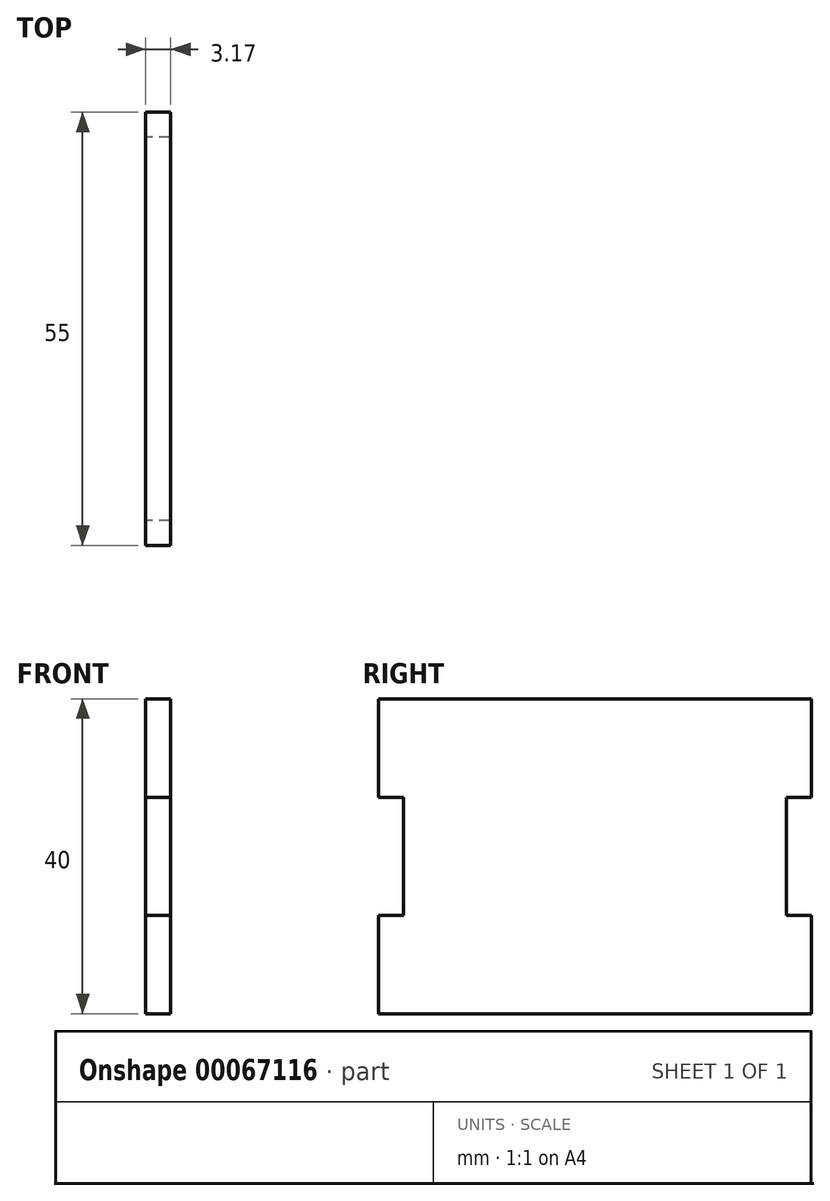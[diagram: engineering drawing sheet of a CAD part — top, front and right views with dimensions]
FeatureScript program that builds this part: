
annotation { "Feature Type Name" : "Feature", "Feature Type Description" : "" }
export const myFeature = defineFeature(function(context is Context, id is Id, definition is map)
    precondition{}
    {
        {
            var Q0;
            Q0=qCreatedBy(makeId("Right.planeOp"),FACE);
            var sketch = newSketch(context, id + "F0", { "sketchPlane" : qUnion([Q0])});
            skLineSegment(sketch, "E0.bottom", {"start": v(-27.5, 0) * mm, "end": v(27.5, 0) * mm});
            skLineSegment(sketch, "E0.top", {"start": v(-27.5, -40) * mm, "end": v(27.5, -40) * mm});
            skLineSegment(sketch, "E0.left", {"start": v(-27.5, 0) * mm, "end": v(-27.5, -40) * mm});
            skLineSegment(sketch, "E0.right", {"start": v(27.5, 0) * mm, "end": v(27.5, -40) * mm});
            skLineSegment(sketch, "E1.bottom", {"start": v(27.5, -12.5) * mm, "end": v(24.32, -12.5) * mm});
            skLineSegment(sketch, "E1.top", {"start": v(27.5, -27.5) * mm, "end": v(24.32, -27.5) * mm});
            skLineSegment(sketch, "E1.left", {"start": v(27.5, -12.5) * mm, "end": v(27.5, -27.5) * mm});
            skLineSegment(sketch, "E1.right", {"start": v(24.32, -12.5) * mm, "end": v(24.32, -27.5) * mm});
            skLineSegment(sketch, "E2.bottom", {"start": v(-27.5, -12.5) * mm, "end": v(-24.32, -12.5) * mm});
            skLineSegment(sketch, "E2.top", {"start": v(-27.5, -27.5) * mm, "end": v(-24.32, -27.5) * mm});
            skLineSegment(sketch, "E2.left", {"start": v(-27.5, -12.5) * mm, "end": v(-27.5, -27.5) * mm});
            skLineSegment(sketch, "E2.right", {"start": v(-24.32, -12.5) * mm, "end": v(-24.32, -27.5) * mm});
            skLineSegment(sketch, "E3.bottom", {"start": v(-10, -40) * mm, "end": v(10, -40) * mm});
            skLineSegment(sketch, "E3.top", {"start": v(-10, -46.35) * mm, "end": v(10, -46.35) * mm});
            skLineSegment(sketch, "E3.left", {"start": v(-10, -40) * mm, "end": v(-10, -46.35) * mm});
            skLineSegment(sketch, "E3.right", {"start": v(10, -40) * mm, "end": v(10, -46.35) * mm});
            skLineSegment(sketch, "E4", {"start": v(-10, -46.35) * mm, "end": v(-27.5, -40) * mm, "construction": true});
            skLineSegment(sketch, "E5", {"start": v(10, -46.35) * mm, "end": v(27.5, -40) * mm, "construction": true});
            skLineSegment(sketch, "E6", {"start": v(24.32, -12.5) * mm, "end": v(24.32, 0) * mm, "construction": true});
            skLineSegment(sketch, "E7", {"start": v(24.32, -27.5) * mm, "end": v(24.32, -40) * mm, "construction": true});
            skSolve(sketch);
        }
        {
            var Q0;
            {var subQ1=sQuery(id+"F0.wireOp",EDGE,"E0.bottom");Q0=makeQuery(id+"F0.imprint","IMPRINT",FACE,{"disambiguationData":[TD([[makeQuery(id+"F0.imprint","IMPRINT",EDGE,{"derivedFrom":subQ1}),-1.0]])]});}
            var Q1;
            Q1=makeQuery(id+"F0.imprint","IMPRINT",FACE,{"disambiguationData":[TD([[makeQuery(id+"F0.imprint","IMPRINT",EDGE,{"derivedFrom":sQuery(id+"F0.wireOp",EDGE,"E3.bottom")}),-1.0]])]});
            extrude(context, id + "F1", {"entities" : qUnion([Q0, Q1]), "depth" : 3.17 * mm});
        }
    });
